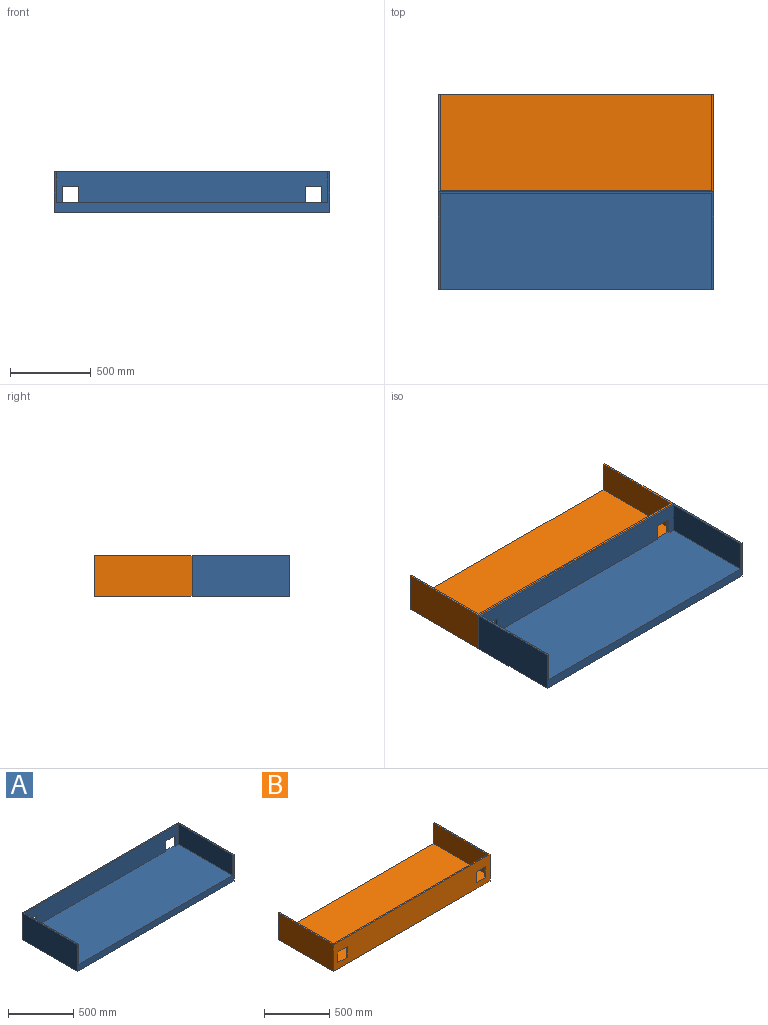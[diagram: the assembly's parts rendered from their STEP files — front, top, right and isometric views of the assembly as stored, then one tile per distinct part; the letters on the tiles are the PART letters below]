
ASSEMBLY  parts=2 mates=1
PART A: 21 faces, bbox 1700x600x250 mm
  f0: plane 1676x191mm, normal (0,-1,0), area 300116mm2, adj f5,f6,f8,f9,f15,f16,f17,f18
  f1: plane 1700x250mm, normal (0,1,0), area 405000mm2, adj f2,f3,f7,f8,f9,f15,f16,f17
  f2: plane 1700x600mm, normal (0,0,-1), area 41076mm2, adj f1,f3,f4,f7,f10,f11,f12,f13
  f3: plane 600x250mm, normal (-1,0,0), area 150000mm2, adj f1,f2,f4,f8
  f4: plane 1700x250mm, normal (0,-1,0), area 104884mm2, adj f2,f3,f5,f6,f7,f8,f9
  f5: plane 588x191mm, normal (1,0,0), area 112308mm2, adj f0,f4,f8,f9
  f6: plane 588x191mm, normal (-1,0,0), area 112308mm2, adj f0,f4,f8,f9
  f7: plane 600x250mm, normal (1,0,0), area 150000mm2, adj f1,f2,f4,f8
  f8: plane 1700x600mm, normal (0,0,1), area 34512mm2, adj f0,f1,f3,f4,f5,f6,f7
  f9: plane 1676x600mm, normal (0,0,1), area 987888mm2, adj f0,f1,f4,f5,f6,f16,f17,f18
  f10: plane 582x50mm, normal (1,0,0), area 29100mm2, adj f2,f11,f13,f14
  f11: plane 1682x50mm, normal (0,1,0), area 84100mm2, adj f2,f10,f12,f14
  f12: plane 582x50mm, normal (-1,0,0), area 29100mm2, adj f2,f11,f13,f14
  f13: plane 1682x50mm, normal (0,-1,0), area 84100mm2, adj f2,f10,f12,f14
  f14: plane 1682x582mm, normal (0,0,-1), area 978924mm2, adj f10,f11,f12,f13
  f15: plane 100x12mm, normal (0,0,-1), area 1200mm2, adj f0,f1,f16,f17
  f16: plane 100x12mm, normal (1,0,0), area 1200mm2, adj f0,f1,f9,f15
  f17: plane 100x12mm, normal (-1,0,0), area 1200mm2, adj f0,f1,f9,f15
  f18: plane 100x12mm, normal (-1,0,0), area 1200mm2, adj f0,f1,f9,f19
  f19: plane 100x12mm, normal (0,0,-1), area 1200mm2, adj f0,f1,f18,f20
  f20: plane 100x12mm, normal (1,0,0), area 1200mm2, adj f0,f1,f9,f19
PART B: 21 faces, bbox 1700x600x250 mm
  f0: plane 1676x191mm, normal (0,1,0), area 300116mm2, adj f5,f6,f8,f9,f15,f16,f17,f18
  f1: plane 1700x250mm, normal (0,-1,0), area 405000mm2, adj f2,f3,f7,f8,f9,f15,f16,f17
  f2: plane 1700x600mm, normal (0,0,-1), area 41076mm2, adj f1,f3,f4,f7,f10,f11,f12,f13
  f3: plane 600x250mm, normal (1,0,0), area 150000mm2, adj f1,f2,f4,f8
  f4: plane 1700x250mm, normal (0,1,0), area 104884mm2, adj f2,f3,f5,f6,f7,f8,f9
  f5: plane 588x191mm, normal (-1,0,0), area 112308mm2, adj f0,f4,f8,f9
  f6: plane 588x191mm, normal (1,0,0), area 112308mm2, adj f0,f4,f8,f9
  f7: plane 600x250mm, normal (-1,0,0), area 150000mm2, adj f1,f2,f4,f8
  f8: plane 1700x600mm, normal (0,0,1), area 34512mm2, adj f0,f1,f3,f4,f5,f6,f7
  f9: plane 1676x600mm, normal (0,0,1), area 987888mm2, adj f0,f1,f4,f5,f6,f16,f17,f18
  f10: plane 582x50mm, normal (-1,0,0), area 29100mm2, adj f2,f11,f13,f14
  f11: plane 1682x50mm, normal (0,-1,0), area 84100mm2, adj f2,f10,f12,f14
  f12: plane 582x50mm, normal (1,0,0), area 29100mm2, adj f2,f11,f13,f14
  f13: plane 1682x50mm, normal (0,1,0), area 84100mm2, adj f2,f10,f12,f14
  f14: plane 1682x582mm, normal (0,0,-1), area 978924mm2, adj f10,f11,f12,f13
  f15: plane 100x12mm, normal (0,0,-1), area 1200mm2, adj f0,f1,f16,f17
  f16: plane 100x12mm, normal (-1,0,0), area 1200mm2, adj f0,f1,f9,f15
  f17: plane 100x12mm, normal (1,0,0), area 1200mm2, adj f0,f1,f9,f15
  f18: plane 100x12mm, normal (1,0,0), area 1200mm2, adj f0,f1,f9,f19
  f19: plane 100x12mm, normal (0,0,-1), area 1200mm2, adj f0,f1,f18,f20
  f20: plane 100x12mm, normal (-1,0,0), area 1200mm2, adj f0,f1,f9,f19
PLACE A t=(-525.68,270.7,-363.22)mm fixed
PLACE B t=(-725.68,270.7,-363.22)mm
MATE revolute B.f3 <-> A.f7  axis (1,0,0) through (1174.32,270.7,-163.22)mm
